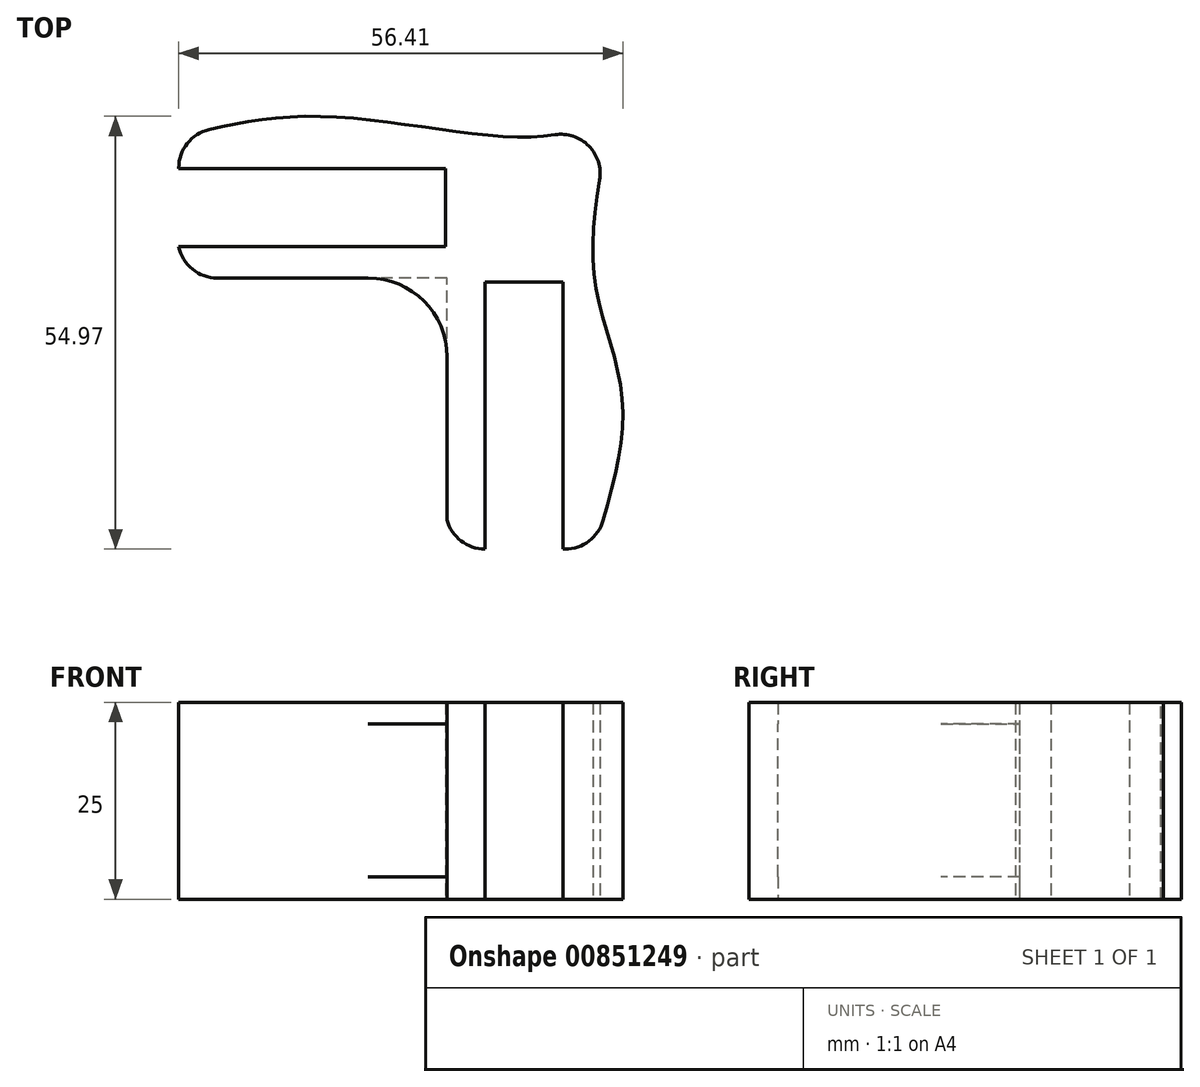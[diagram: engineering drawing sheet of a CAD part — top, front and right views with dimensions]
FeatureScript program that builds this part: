
annotation { "Feature Type Name" : "Feature", "Feature Type Description" : "" }
export const myFeature = defineFeature(function(context is Context, id is Id, definition is map)
    precondition{}
    {
        {
            var Q0;
            Q0=qCreatedBy(makeId("Top.planeOp"),FACE);
            var sketch = newSketch(context, id + "F0", { "sketchPlane" : qUnion([Q0])});
            skLineSegment(sketch, "E0.bottom", {"start": v(46.13, 46.63) * mm, "end": v(-43.87, 46.63) * mm, "construction": true});
            skLineSegment(sketch, "E0.top", {"start": v(46.13, -43.37) * mm, "end": v(-43.87, -43.37) * mm, "construction": true});
            skLineSegment(sketch, "E0.left", {"start": v(46.13, 46.63) * mm, "end": v(46.13, -43.37) * mm, "construction": true});
            skLineSegment(sketch, "E1", {"start": v(4.96, -9.48) * mm, "end": v(4.96, -43.37) * mm});
            skLineSegment(sketch, "E2", {"start": v(-4.96, -9.48) * mm, "end": v(-4.96, -43.37) * mm});
            skLineSegment(sketch, "E3", {"start": v(-10, 4.96) * mm, "end": v(-43.87, 4.96) * mm});
            skLineSegment(sketch, "E4", {"start": v(-10, -4.96) * mm, "end": v(-43.87, -4.96) * mm});
            skLineSegment(sketch, "E5", {"start": v(-10, -4.96) * mm, "end": v(-10, 4.96) * mm});
            skLineSegment(sketch, "E6", {"start": v(-4.96, -9.48) * mm, "end": v(4.96, -9.48) * mm});
            skLineSegment(sketch, "E7", {"start": v(-43.87, -4.96) * mm, "end": v(-43.87, -8.96) * mm});
            skLineSegment(sketch, "E8", {"start": v(-4.96, -43.37) * mm, "end": v(-4.97, -43.37) * mm});
            skLineSegment(sketch, "E9", {"start": v(-43.87, 4.96) * mm, "end": v(-43.87, 8.96) * mm});
            skLineSegment(sketch, "E10", {"start": v(4.96, -43.37) * mm, "end": v(8.96, -43.37) * mm});
            skFitSpline(sketch, "E11", {"points": [v(-43.87, 8.96) * mm, v(-25.72, 11.58) * mm, v(0, 8.96) * mm, v(11.1, 11.21) * mm], "startDerivative": vector(49.68, 12.5) * mm, "endDerivative": vector(36.5, 12.65) * mm});
            skFitSpline(sketch, "E12", {"points": [v(8.96, -43.37) * mm, v(12.48, -24.43) * mm, v(8.96, -8.93) * mm, v(11.1, 11.21) * mm], "startDerivative": vector(17.47, 57.6) * mm, "endDerivative": vector(12.47, 60.14) * mm});
            skLineSegment(sketch, "E13.bottom", {"start": v(24.76, 22.31) * mm, "end": v(24.23, 22.31) * mm});
            skLineSegment(sketch, "E13.top", {"start": v(24.76, -47.4) * mm, "end": v(24.23, -47.4) * mm});
            skPoint(sketch, "E14.visualSharp", {"position": v(-8.96, -43.37) * mm});
            skArc(sketch, "E14.filletArc", {"start": v(-9.8, -39.69) * mm, "mid": v(-8, -42.35) * mm, "end": v(-4.97, -43.37) * mm});
            skLineSegment(sketch, "E15", {"start": v(-43.87, -8.96) * mm, "end": v(-9.8, -8.96) * mm});
            skLineSegment(sketch, "E16", {"start": v(-9.8, -8.96) * mm, "end": v(-9.8, -39.69) * mm});
            skSolve(sketch);
        }
        {
            var Q0;
            Q0=qSketchRegion(id+"F0",true);
            extrude(context, id + "F1", {"entities" : qUnion([Q0]), "depth" : 25 * mm, "offsetDistance" : 25 * mm});
        }
        {
            var Q0;
            Q0=makeQuery(id+"F1.opExtrude","SWEPT_EDGE",EDGE,{"disambiguationData":[OSD([sQuery(id+"F0.wireOp",EDGE,"E10"),sQuery(id+"F0.wireOp",EDGE,"E12")])]});
            var Q1;
            Q1=makeQuery(id+"F1.opExtrude","SWEPT_EDGE",EDGE,{"disambiguationData":[OSD([sQuery(id+"F0.wireOp",EDGE,"E11"),sQuery(id+"F0.wireOp",EDGE,"E12")])]});
            var Q2;
            Q2=makeQuery(id+"F1.opExtrude","SWEPT_EDGE",EDGE,{"disambiguationData":[OSD([sQuery(id+"F0.wireOp",EDGE,"E9"),sQuery(id+"F0.wireOp",EDGE,"E11")])]});
            fillet(context, id + "F2", {"entities" : qUnion([Q0, Q1, Q2]), "radius" : 5 * mm, "tangentPropagation" : true, "allowEdgeOverflow" : false});
        }
        {
            var Q0;
            Q0=makeQuery(id+"F1.opExtrude","SWEPT_EDGE",EDGE,{"disambiguationData":[OSD([sQuery(id+"F0.wireOp",EDGE,"E15"),sQuery(id+"F0.wireOp",EDGE,"E16")])]});
            fillet(context, id + "F3", {"entities" : qUnion([Q0]), "radius" : 10 * mm, "tangentPropagation" : true, "allowEdgeOverflow" : false});
        }
        {
            var Q0;
            Q0=makeQuery(id+"F1.opExtrude","SWEPT_FACE",FACE,{"disambiguationData":[OSD([sQuery(id+"F0.wireOp",EDGE,"E7")])]});
            var sketch = newSketch(context, id + "F4", { "sketchPlane" : qUnion([Q0])});
            skLineSegment(sketch, "E17.bottom", {"start": v(8.96, 22.3) * mm, "end": v(39.7, 22.3) * mm});
            skLineSegment(sketch, "E17.top", {"start": v(8.96, 2.85) * mm, "end": v(39.7, 2.85) * mm});
            skLineSegment(sketch, "E17.left", {"start": v(8.96, 22.3) * mm, "end": v(8.96, 2.85) * mm});
            skLineSegment(sketch, "E17.right", {"start": v(39.7, 22.3) * mm, "end": v(39.7, 2.85) * mm});
            skSolve(sketch);
        }
        {
            var Q0;
            Q0=makeQuery(id+"F4.imprint","IMPRINT",FACE,{"disambiguationData":[TD([[makeQuery(id+"F4.imprint","IMPRINT",EDGE,{"derivedFrom":sQuery(id+"F4.wireOp",EDGE,"E17.bottom")}),-1.0]])]});
            extrude(context, id + "F5", {"entities" : qUnion([Q0]), "operationType" : NewBodyOperationType.REMOVE, "oppositeDirection" : true, "depth" : 34.08 * mm, "offsetDistance" : 25 * mm});
        }
        {
            var Q0;
            Q0=makeQuery(id+"F1.opExtrude","SWEPT_EDGE",EDGE,{"disambiguationData":[OSD([sQuery(id+"F0.wireOp",EDGE,"E7"),sQuery(id+"F0.wireOp",EDGE,"E15")])]});
            fillet(context, id + "F6", {"entities" : qUnion([Q0]), "radius" : 5 * mm, "tangentPropagation" : true, "allowEdgeOverflow" : false});
        }
    });
